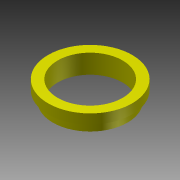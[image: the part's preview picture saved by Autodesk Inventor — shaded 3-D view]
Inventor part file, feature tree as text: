
AUTODESK INVENTOR PART (.ipt)
format: ipt  version: 2011 (Build 150239000, 239)  size: 86,016 bytes
history: native  units: in
note: dims shown in document units (in); Inventor stores cm internally (conversion verified against a paired STEP export)
features: revolve x1, sketch x1
ambient origin geometry x8: Origin, YZ Plane, XZ Plane, XY Plane, X Axis, Y Axis, Z Axis, Center Point
bodies: Solid1 (feature_tree)
feature tree (2):
  revolve  "Revolution1"  [1 undecoded]
  sketch  "Sketch1"  dims[d0=0.125in d1=0.125in d4=0.55in d5=90.0deg d6=0.125in]
note: 1 required parameter value undecoded (feature->parameter linkage not recoverable at this tier; creation-order binding heuristic only, values carry confidence <= 0.55)
